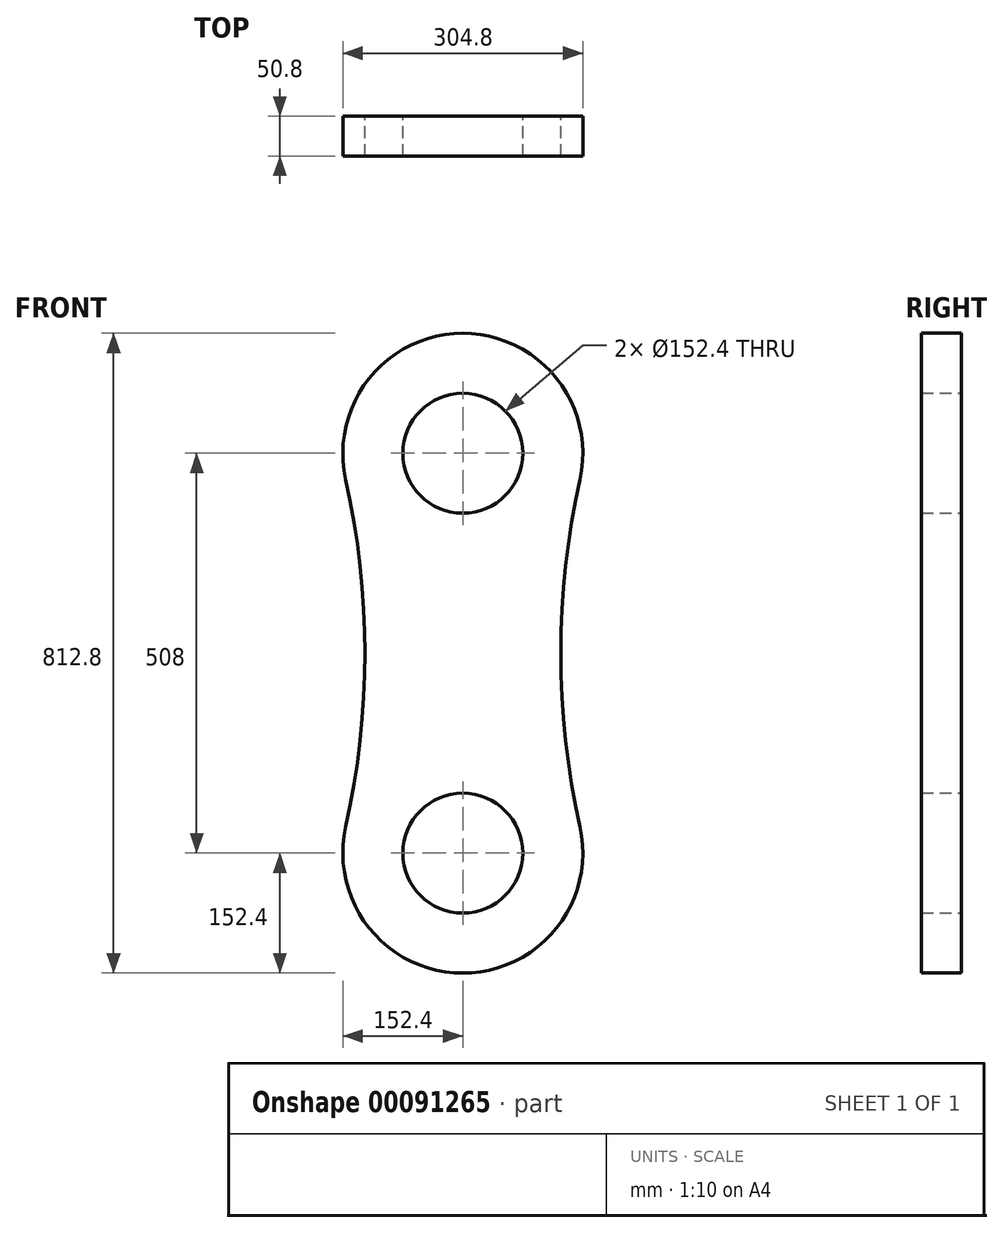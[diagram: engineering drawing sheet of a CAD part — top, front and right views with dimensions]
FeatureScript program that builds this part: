
annotation { "Feature Type Name" : "Feature", "Feature Type Description" : "" }
export const myFeature = defineFeature(function(context is Context, id is Id, definition is map)
    precondition{}
    {
        {
            var Q0;
            Q0=qCreatedBy(makeId("Front.planeOp"),FACE);
            var sketch = newSketch(context, id + "F0", { "sketchPlane" : qUnion([Q0])});
            skArc(sketch, "E0", {"start": v(-148.76, 33.13) * mm, "mid": v(0, -152.4) * mm, "end": v(148.76, 33.13) * mm});
            skArc(sketch, "E1", {"start": v(148.76, 474.87) * mm, "mid": v(0, 660.4) * mm, "end": v(-148.76, 474.87) * mm});
            skArc(sketch, "E2", {"start": v(-148.76, 33.13) * mm, "mid": v(-124.46, 254) * mm, "end": v(-148.76, 474.87) * mm});
            skArc(sketch, "E3", {"start": v(148.76, 474.87) * mm, "mid": v(124.46, 254) * mm, "end": v(148.76, 33.13) * mm});
            skCircle(sketch, "E4", {"center": v(0, 0) * mm, "radius": 76.2 * mm});
            skCircle(sketch, "E5", {"center": v(0, 508) * mm, "radius": 76.2 * mm});
            skSolve(sketch);
        }
        {
            var Q0;
            Q0=makeQuery(id+"F0.imprint","IMPRINT",FACE,{"disambiguationData":[TD([[makeQuery(id+"F0.imprint","IMPRINT",EDGE,{"derivedFrom":sQuery(id+"F0.wireOp",EDGE,"E0")}),1.0]])]});
            extrude(context, id + "F1", {"entities" : qUnion([Q0]), "depth" : 50.8 * mm});
        }
    });
